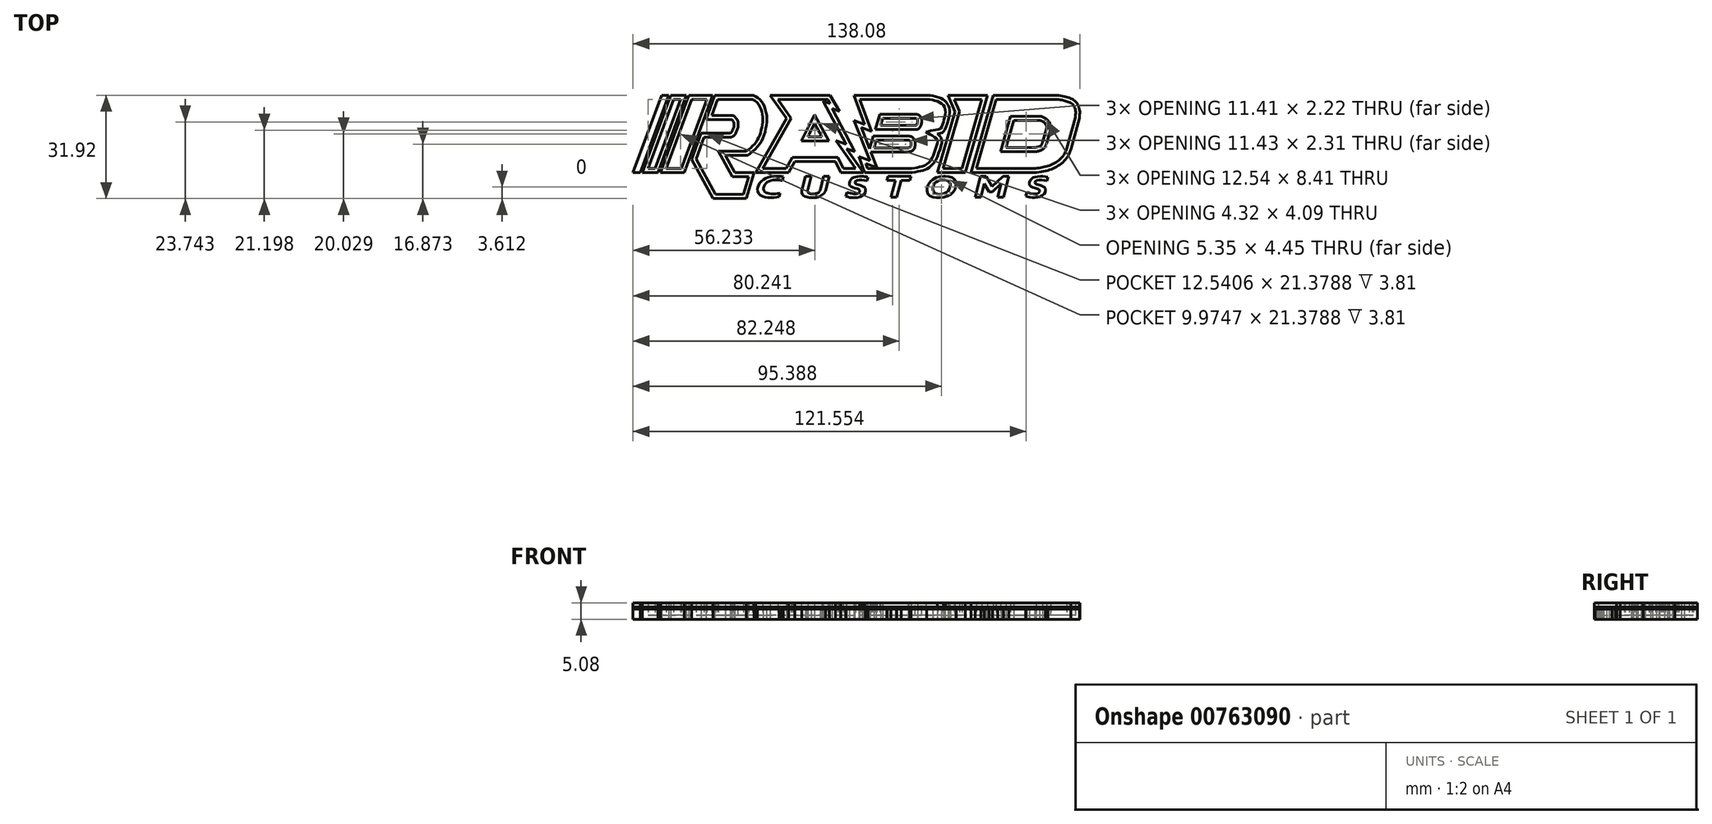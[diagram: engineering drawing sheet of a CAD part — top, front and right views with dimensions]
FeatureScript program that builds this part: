
annotation { "Feature Type Name" : "Feature", "Feature Type Description" : "" }
export const myFeature = defineFeature(function(context is Context, id is Id, definition is map)
    precondition{}
    {
        {
            var Q0;
            Q0=qCreatedBy(makeId("Top.planeOp"),FACE);
            var sketch = newSketch(context, id + "F0", { "sketchPlane" : qUnion([Q0])});
            skLineSegment(sketch, "E0", {"start": v(63.14, 15.4) * mm, "end": v(43.59, 15.4) * mm});
            skLineSegment(sketch, "E1", {"start": v(-67.72, -8.52) * mm, "end": v(-58.92, 15.4) * mm});
            skLineSegment(sketch, "E2", {"start": v(-51.92, -8.52) * mm, "end": v(-59.3, -8.52) * mm});
            skLineSegment(sketch, "E3", {"start": v(-56.72, 15.4) * mm, "end": v(-65.52, -8.52) * mm});
            skLineSegment(sketch, "E4", {"start": v(-64.84, -8.52) * mm, "end": v(-56.04, 15.4) * mm});
            skLineSegment(sketch, "E5", {"start": v(-51.23, 15.4) * mm, "end": v(-60.03, -8.52) * mm});
            skLineSegment(sketch, "E6", {"start": v(-59.3, -8.52) * mm, "end": v(-50.5, 15.4) * mm});
            skLineSegment(sketch, "E7", {"start": v(-43.12, 15.4) * mm, "end": v(-51.92, -8.52) * mm});
            skLineSegment(sketch, "E8", {"start": v(-45.2, 7.94) * mm, "end": v(-42.45, 15.4) * mm});
            skLineSegment(sketch, "E9", {"start": v(-45.2, 7.94) * mm, "end": v(-37.2, 7.94) * mm});
            skLineSegment(sketch, "E10", {"start": v(-37.63, 3.75) * mm, "end": v(-46.65, 3.75) * mm});
            skLineSegment(sketch, "E11", {"start": v(-46.65, 3.75) * mm, "end": v(-49.65, -4.39) * mm});
            skLineSegment(sketch, "E12", {"start": v(-49.65, -4.39) * mm, "end": v(-43.04, -16.52) * mm});
            skLineSegment(sketch, "E13", {"start": v(-43.04, -16.52) * mm, "end": v(-32.71, -16.52) * mm});
            skLineSegment(sketch, "E14", {"start": v(-32.71, -16.52) * mm, "end": v(-30.27, -8.46) * mm});
            skLineSegment(sketch, "E15", {"start": v(-30.27, -8.46) * mm, "end": v(-36.23, -8.46) * mm});
            skLineSegment(sketch, "E16", {"start": v(-36.23, -8.46) * mm, "end": v(-39.16, -3.08) * mm});
            skLineSegment(sketch, "E17", {"start": v(-39.16, -3.08) * mm, "end": v(-32.26, -3.08) * mm});
            skLineSegment(sketch, "E18", {"start": v(-29.78, -8.46) * mm, "end": v(-19.63, -8.46) * mm});
            skLineSegment(sketch, "E19", {"start": v(-25.33, 15.4) * mm, "end": v(-20.3, 8.28) * mm});
            skLineSegment(sketch, "E20", {"start": v(-20.3, 8.28) * mm, "end": v(-29.78, -8.46) * mm});
            skLineSegment(sketch, "E21", {"start": v(-19.63, -8.46) * mm, "end": v(-17.7, -5.04) * mm});
            skLineSegment(sketch, "E22", {"start": v(-17.7, -5.04) * mm, "end": v(-5.2, -5.04) * mm});
            skLineSegment(sketch, "E23", {"start": v(-5.2, -5.04) * mm, "end": v(-3.5, -8.46) * mm});
            skLineSegment(sketch, "E24", {"start": v(-6.75, 15.4) * mm, "end": v(-3.93, 10.47) * mm});
            skLineSegment(sketch, "E25", {"start": v(-3.93, 10.47) * mm, "end": v(-6.2, 11.32) * mm});
            skLineSegment(sketch, "E26", {"start": v(-6.2, 11.32) * mm, "end": v(0.84, -1.97) * mm});
            skLineSegment(sketch, "E27", {"start": v(0.84, -1.97) * mm, "end": v(-1.66, -1.06) * mm});
            skLineSegment(sketch, "E28", {"start": v(-1.66, -1.06) * mm, "end": v(3.5, -8.46) * mm});
            skLineSegment(sketch, "E29", {"start": v(-9.33, 2.63) * mm, "end": v(-13.65, 2.63) * mm});
            skLineSegment(sketch, "E30", {"start": v(-13.65, 2.63) * mm, "end": v(-11.6, 6.72) * mm});
            skLineSegment(sketch, "E31", {"start": v(-11.6, 6.72) * mm, "end": v(-9.33, 2.63) * mm});
            skLineSegment(sketch, "E32", {"start": v(0.59, 15.4) * mm, "end": v(3.85, 6.44) * mm});
            skLineSegment(sketch, "E33", {"start": v(3.85, 6.44) * mm, "end": v(0.55, 7.69) * mm});
            skLineSegment(sketch, "E34", {"start": v(0.55, 7.69) * mm, "end": v(5.5, -4.8) * mm});
            skLineSegment(sketch, "E35", {"start": v(5.5, -4.8) * mm, "end": v(2.03, -3.56) * mm});
            skLineSegment(sketch, "E36", {"start": v(2.03, -3.56) * mm, "end": v(3.9, -8.46) * mm});
            skLineSegment(sketch, "E37", {"start": v(9.47, 8.33) * mm, "end": v(8.82, 6.12) * mm});
            skLineSegment(sketch, "E38", {"start": v(6.8, -0.8) * mm, "end": v(17.35, -0.8) * mm});
            skLineSegment(sketch, "E39", {"start": v(7.48, 1.5) * mm, "end": v(17.6, 1.5) * mm});
            skLineSegment(sketch, "E40", {"start": v(9.47, 8.33) * mm, "end": v(19.75, 8.33) * mm});
            skLineSegment(sketch, "E41", {"start": v(8.82, 6.12) * mm, "end": v(19.5, 6.12) * mm});
            skLineSegment(sketch, "E42", {"start": v(29.63, 15.4) * mm, "end": v(31.86, 10.36) * mm});
            skLineSegment(sketch, "E43", {"start": v(31.86, 10.36) * mm, "end": v(26.4, -8.46) * mm});
            skLineSegment(sketch, "E44", {"start": v(41.79, 15.4) * mm, "end": v(34.96, -8.46) * mm});
            skLineSegment(sketch, "E45", {"start": v(43.59, 15.4) * mm, "end": v(36.77, -8.46) * mm});
            skLineSegment(sketch, "E46", {"start": v(57.72, 7.72) * mm, "end": v(49.97, 7.72) * mm});
            skLineSegment(sketch, "E47", {"start": v(49.97, 7.72) * mm, "end": v(47.56, -0.7) * mm});
            skLineSegment(sketch, "E48", {"start": v(47.56, -0.7) * mm, "end": v(56.76, -0.7) * mm});
            skLineSegment(sketch, "E49", {"start": v(60.1, 5.21) * mm, "end": v(58.87, 0.9) * mm});
            skFitSpline(sketch, "E50", {"points": [v(70.23, 8.37) * mm, v(70.23, 11.3) * mm, v(68.98, 13.62) * mm, v(67.2, 14.63) * mm, v(63.14, 15.4) * mm], "startDerivative": vector(1.44, 11.8) * mm, "endDerivative": vector(-15.36, 0) * mm});
            skLineSegment(sketch, "E51", {"start": v(70.23, 8.37) * mm, "end": v(67.61, -1.4) * mm});
            skFitSpline(sketch, "E52", {"points": [v(26.31, 3.48) * mm, v(27.66, 3.78) * mm, v(28.6, 4.72) * mm, v(30.1, 9.84) * mm, v(29.74, 12.25) * mm, v(28.71, 13.68) * mm, v(26.6, 14.85) * mm, v(23.32, 15.4) * mm], "startDerivative": vector(12.7, 2.15) * mm, "endDerivative": vector(-17.65, 0) * mm});
            skFitSpline(sketch, "E53", {"points": [v(26.31, 3.48) * mm, v(27.17, 2.79) * mm, v(27.7, 1.55) * mm, v(27.61, 0.35) * mm, v(25.8, -4.7) * mm, v(24.38, -6.43) * mm, v(22.74, -7.53) * mm, v(20.7, -8.07) * mm, v(17.69, -8.46) * mm], "startDerivative": vector(10.33, -6.33) * mm, "endDerivative": vector(-21.35, 0) * mm});
            skFitSpline(sketch, "E54", {"points": [v(19.75, 8.33) * mm, v(20.01, 8.2) * mm, v(20.22, 7.86) * mm, v(20.1, 6.56) * mm, v(19.95, 6.28) * mm, v(19.5, 6.12) * mm], "startDerivative": vector(1.94, 0) * mm, "endDerivative": vector(-2.82, 0) * mm});
            skFitSpline(sketch, "E55", {"points": [v(17.6, 1.5) * mm, v(17.93, 1.37) * mm, v(18.17, 0.96) * mm, v(18.18, -0.17) * mm, v(17.97, -0.55) * mm, v(17.35, -0.8) * mm], "startDerivative": vector(2.34, 0) * mm, "endDerivative": vector(-5.47, -0.56) * mm});
            skFitSpline(sketch, "E56", {"points": [v(-30.5, 15.4) * mm, v(-28.7, 14.3) * mm, v(-27.34, 12.4) * mm, v(-26.4, 9.2) * mm, v(-26.57, 5.78) * mm, v(-27.6, 2.09) * mm, v(-29.64, -0.93) * mm, v(-32.26, -3.08) * mm], "startDerivative": vector(16.3, -8.18) * mm, "endDerivative": vector(-18.4, -13.35) * mm});
            skFitSpline(sketch, "E57", {"points": [v(57.72, 7.72) * mm, v(58.57, 7.52) * mm, v(59.23, 7.13) * mm, v(59.76, 6.54) * mm, v(60.1, 5.21) * mm], "startDerivative": vector(3.5, 0) * mm, "endDerivative": vector(-0.84, -6.8) * mm});
            skFitSpline(sketch, "E58", {"points": [v(56.76, -0.7) * mm, v(57.5, -0.52) * mm, v(58.2, -0.25) * mm, v(58.63, 0.26) * mm, v(58.87, 0.9) * mm], "startDerivative": vector(2.87, 0.64) * mm, "endDerivative": vector(0.84, 2.68) * mm});
            skLineSegment(sketch, "E59.trimOffspring", {"start": v(-56.72, 15.4) * mm, "end": v(-58.92, 15.4) * mm});
            skLineSegment(sketch, "E60.trimOffspring", {"start": v(-51.23, 15.4) * mm, "end": v(-56.04, 15.4) * mm});
            skLineSegment(sketch, "E61.trimOffspring", {"start": v(-43.12, 15.4) * mm, "end": v(-50.5, 15.4) * mm});
            skLineSegment(sketch, "E62.trimOffspring", {"start": v(-30.5, 15.4) * mm, "end": v(-42.45, 15.4) * mm});
            skLineSegment(sketch, "E63.trimOffspring", {"start": v(-60.03, -8.52) * mm, "end": v(-64.84, -8.52) * mm});
            skLineSegment(sketch, "E64.trimOffspring", {"start": v(-65.52, -8.52) * mm, "end": v(-67.72, -8.52) * mm});
            skLineSegment(sketch, "E65.trimOffspring", {"start": v(-3.5, -8.46) * mm, "end": v(3.5, -8.46) * mm});
            skLineSegment(sketch, "E66.trimOffspring", {"start": v(3.9, -8.46) * mm, "end": v(17.69, -8.46) * mm});
            skLineSegment(sketch, "E67.trimOffspring", {"start": v(-6.75, 15.4) * mm, "end": v(-25.33, 15.4) * mm});
            skLineSegment(sketch, "E68.trimOffspring", {"start": v(7.48, 1.5) * mm, "end": v(6.8, -0.8) * mm});
            skLineSegment(sketch, "E69.trimOffspring", {"start": v(23.32, 15.4) * mm, "end": v(0.59, 15.4) * mm});
            skLineSegment(sketch, "E70.trimOffspring", {"start": v(26.4, -8.46) * mm, "end": v(34.96, -8.46) * mm});
            skLineSegment(sketch, "E71.trimOffspring", {"start": v(36.77, -8.46) * mm, "end": v(56.13, -8.46) * mm});
            skLineSegment(sketch, "E72.trimOffspring", {"start": v(41.79, 15.4) * mm, "end": v(29.63, 15.4) * mm});
            skFitSpline(sketch, "E73", {"points": [v(67.61, -1.4) * mm, v(66.86, -3.06) * mm, v(65.63, -4.79) * mm, v(63.85, -6.28) * mm, v(61.91, -7.32) * mm, v(59.62, -7.97) * mm, v(56.13, -8.46) * mm], "startDerivative": vector(-4.7, -11.34) * mm, "endDerivative": vector(-18.16, 0) * mm});
            skLineSegment(sketch, "E74", {"start": v(-21.23, -9.76) * mm, "end": v(-21.5, -10.99) * mm});
            skFitSpline(sketch, "E75", {"points": [v(-21.5, -10.99) * mm, v(-22.97, -10.72) * mm, v(-24.28, -10.74) * mm, v(-25.85, -11.2) * mm, v(-27, -12.23) * mm, v(-27.37, -13.14) * mm, v(-27.28, -13.97) * mm, v(-26.77, -14.6) * mm, v(-25.82, -14.94) * mm, v(-24.18, -15.08) * mm, v(-22.33, -14.83) * mm], "startDerivative": vector(-13.97, 2.96) * mm, "endDerivative": vector(15.34, 2.82) * mm});
            skFitSpline(sketch, "E76", {"points": [v(-21.23, -9.76) * mm, v(-22.2, -9.6) * mm, v(-23.42, -9.55) * mm, v(-24.64, -9.6) * mm, v(-26.04, -9.93) * mm, v(-26.99, -10.35) * mm, v(-27.96, -11) * mm, v(-28.75, -12) * mm, v(-29.08, -12.73) * mm, v(-29.23, -13.4) * mm, v(-29.15, -14.32) * mm, v(-28.73, -15.14) * mm, v(-27.9, -15.77) * mm, v(-26.68, -16.15) * mm, v(-25.33, -16.25) * mm, v(-23.8, -16.2) * mm, v(-22.58, -15.95) * mm], "startDerivative": vector(-16.16, 3.13) * mm, "endDerivative": vector(17.8, 4.48) * mm});
            skLineSegment(sketch, "E77.trimOffspring", {"start": v(-22.33, -14.83) * mm, "end": v(-22.58, -15.95) * mm});
            skLineSegment(sketch, "E78", {"start": v(-14.42, -9.63) * mm, "end": v(-12.66, -9.63) * mm});
            skLineSegment(sketch, "E79", {"start": v(12.2, -16.1) * mm, "end": v(13.8, -16.1) * mm});
            skLineSegment(sketch, "E80", {"start": v(-14.42, -9.63) * mm, "end": v(-15.45, -13.6) * mm});
            skLineSegment(sketch, "E81", {"start": v(-12.66, -9.63) * mm, "end": v(-13.72, -13.7) * mm});
            skLineSegment(sketch, "E82", {"start": v(-8.8, -9.63) * mm, "end": v(-9.9, -13.88) * mm});
            skLineSegment(sketch, "E83", {"start": v(-7.1, -9.63) * mm, "end": v(-8.22, -14.01) * mm});
            skFitSpline(sketch, "E84", {"points": [v(-15.45, -13.6) * mm, v(-15.56, -14.25) * mm, v(-15.45, -14.91) * mm, v(-15.19, -15.4) * mm, v(-14.47, -15.9) * mm, v(-13.08, -16.2) * mm, v(-11.72, -16.22) * mm, v(-10.7, -16.06) * mm, v(-9.8, -15.69) * mm, v(-8.93, -15.06) * mm, v(-8.47, -14.55) * mm, v(-8.22, -14.01) * mm], "startDerivative": vector(-1.99, -8.13) * mm, "endDerivative": vector(2.8, 7.52) * mm});
            skFitSpline(sketch, "E85", {"points": [v(-13.72, -13.7) * mm, v(-13.77, -13.94) * mm, v(-13.77, -14.2) * mm, v(-13.72, -14.43) * mm, v(-13.43, -14.76) * mm, v(-12.93, -14.99) * mm, v(-11.88, -15.05) * mm, v(-11.08, -14.96) * mm, v(-10.47, -14.73) * mm, v(-10.11, -14.34) * mm, v(-9.9, -13.88) * mm], "startDerivative": vector(-0.84, -3.35) * mm, "endDerivative": vector(1.84, 4.68) * mm});
            skLineSegment(sketch, "E86.trimOffspring", {"start": v(-8.8, -9.63) * mm, "end": v(-7.1, -9.63) * mm});
            skLineSegment(sketch, "E87", {"start": v(4.85, -9.89) * mm, "end": v(4.6, -11.04) * mm});
            skFitSpline(sketch, "E88", {"points": [v(4.6, -11.04) * mm, v(3.56, -10.81) * mm, v(2.6, -10.7) * mm, v(1.85, -10.74) * mm, v(1.26, -10.94) * mm, v(1, -11.17) * mm, v(0.94, -11.35) * mm, v(0.93, -11.6) * mm, v(1.06, -11.85) * mm, v(1.45, -12.06) * mm, v(2.83, -12.5) * mm, v(3.5, -12.8) * mm, v(3.91, -13.1) * mm, v(4.11, -13.37) * mm, v(4.17, -13.67) * mm, v(4.17, -14.01) * mm, v(4.02, -14.62) * mm, v(3.54, -15.3) * mm, v(2.88, -15.77) * mm, v(2.05, -16.06) * mm, v(0.97, -16.24) * mm, v(0.23, -16.27) * mm, v(-0.68, -16.14) * mm, v(-1.44, -15.96) * mm, v(-1.98, -15.77) * mm], "startDerivative": vector(-19.24, 4.6) * mm, "endDerivative": vector(-13.06, 4.98) * mm});
            skFitSpline(sketch, "E89", {"points": [v(4.85, -9.89) * mm, v(4.17, -9.74) * mm, v(3.28, -9.63) * mm, v(2.3, -9.63) * mm, v(1.36, -9.74) * mm, v(0.64, -9.93) * mm, v(0.14, -10.19) * mm, v(-0.27, -10.55) * mm, v(-0.68, -11.1) * mm, v(-0.87, -11.73) * mm, v(-0.72, -12.43) * mm, v(-0.15, -12.87) * mm, v(0.52, -13.13) * mm, v(1.58, -13.47) * mm, v(2.06, -13.67) * mm, v(2.33, -14) * mm, v(2.36, -14.28) * mm, v(2.25, -14.6) * mm, v(1.98, -14.81) * mm, v(1.59, -14.98) * mm, v(0.9, -15.06) * mm, v(0.29, -15.02) * mm, v(-0.54, -14.88) * mm, v(-1.25, -14.69) * mm, v(-1.63, -14.5) * mm], "startDerivative": vector(-14.34, 3.67) * mm, "endDerivative": vector(-10.03, 5.5) * mm});
            skLineSegment(sketch, "E90", {"start": v(-1.63, -14.5) * mm, "end": v(-1.98, -15.77) * mm});
            skLineSegment(sketch, "E91", {"start": v(60.47, -9.88) * mm, "end": v(60.23, -11.03) * mm});
            skFitSpline(sketch, "E92", {"points": [v(60.23, -11.03) * mm, v(59.18, -10.8) * mm, v(58.22, -10.69) * mm, v(57.47, -10.73) * mm, v(56.88, -10.93) * mm, v(56.62, -11.16) * mm, v(56.56, -11.34) * mm, v(56.55, -11.6) * mm, v(56.68, -11.84) * mm, v(57.07, -12.06) * mm, v(58.45, -12.5) * mm, v(59.12, -12.8) * mm, v(59.53, -13.08) * mm, v(59.73, -13.36) * mm, v(59.79, -13.67) * mm, v(59.79, -14) * mm, v(59.64, -14.61) * mm, v(59.16, -15.29) * mm, v(58.5, -15.76) * mm, v(57.67, -16.06) * mm, v(56.59, -16.24) * mm, v(55.85, -16.26) * mm, v(54.94, -16.13) * mm, v(54.19, -15.95) * mm, v(53.64, -15.76) * mm], "startDerivative": vector(-19.24, 4.6) * mm, "endDerivative": vector(-13.06, 4.98) * mm});
            skFitSpline(sketch, "E93", {"points": [v(60.47, -9.88) * mm, v(59.79, -9.73) * mm, v(58.9, -9.62) * mm, v(57.92, -9.62) * mm, v(56.98, -9.73) * mm, v(56.26, -9.92) * mm, v(55.76, -10.18) * mm, v(55.35, -10.54) * mm, v(54.94, -11.1) * mm, v(54.75, -11.73) * mm, v(54.9, -12.43) * mm, v(55.47, -12.86) * mm, v(56.14, -13.12) * mm, v(57.2, -13.46) * mm, v(57.68, -13.67) * mm, v(57.95, -14) * mm, v(57.99, -14.27) * mm, v(57.87, -14.6) * mm, v(57.6, -14.8) * mm, v(57.2, -14.97) * mm, v(56.52, -15.05) * mm, v(55.91, -15) * mm, v(55.08, -14.87) * mm, v(54.37, -14.68) * mm, v(54, -14.5) * mm], "startDerivative": vector(-14.34, 3.67) * mm, "endDerivative": vector(-10.03, 5.5) * mm});
            skLineSegment(sketch, "E94", {"start": v(54, -14.5) * mm, "end": v(53.64, -15.76) * mm});
            skLineSegment(sketch, "E95", {"start": v(11.08, -9.63) * mm, "end": v(10.77, -10.85) * mm});
            skLineSegment(sketch, "E96", {"start": v(10.77, -10.85) * mm, "end": v(13.42, -10.85) * mm});
            skLineSegment(sketch, "E97", {"start": v(13.42, -10.85) * mm, "end": v(12.02, -16.1) * mm});
            skLineSegment(sketch, "E98", {"start": v(12.02, -16.1) * mm, "end": v(12.2, -16.1) * mm});
            skLineSegment(sketch, "E99", {"start": v(13.8, -16.1) * mm, "end": v(15.2, -10.85) * mm});
            skLineSegment(sketch, "E100", {"start": v(15.2, -10.85) * mm, "end": v(17.86, -10.85) * mm});
            skLineSegment(sketch, "E101", {"start": v(17.86, -10.85) * mm, "end": v(18.16, -9.63) * mm});
            skFitSpline(sketch, "E102", {"points": [v(27.98, -10.68) * mm, v(27.19, -10.76) * mm, v(26.47, -11.02) * mm, v(25.85, -11.42) * mm, v(25.4, -11.93) * mm, v(25.08, -12.64) * mm, v(24.92, -13.24) * mm, v(24.96, -14) * mm, v(25.34, -14.58) * mm, v(25.9, -14.94) * mm, v(26.64, -15.1) * mm, v(27.47, -15.13) * mm, v(28.26, -14.98) * mm, v(29.06, -14.64) * mm, v(29.68, -14.13) * mm, v(30.1, -13.5) * mm, v(30.34, -12.7) * mm, v(30.37, -12.02) * mm, v(30.16, -11.45) * mm, v(29.8, -11.09) * mm, v(29.2, -10.83) * mm, v(28.61, -10.7) * mm, v(27.98, -10.68) * mm]});
            skFitSpline(sketch, "E103", {"points": [v(28.21, -9.63) * mm, v(27.44, -9.67) * mm, v(26.74, -9.79) * mm, v(25.84, -10.1) * mm, v(25.14, -10.46) * mm, v(24.5, -10.9) * mm, v(24.01, -11.4) * mm, v(23.65, -11.96) * mm, v(23.35, -12.55) * mm, v(23.16, -13.25) * mm, v(23.1, -13.88) * mm, v(23.2, -14.57) * mm, v(23.4, -15.05) * mm, v(23.77, -15.47) * mm, v(24.22, -15.73) * mm, v(24.84, -15.98) * mm, v(25.5, -16.1) * mm, v(26.21, -16.15) * mm, v(27.08, -16.16) * mm, v(27.82, -16.14) * mm, v(28.85, -15.98) * mm, v(29.51, -15.73) * mm, v(30.26, -15.31) * mm, v(30.74, -15) * mm, v(31.25, -14.48) * mm, v(31.62, -13.96) * mm, v(31.88, -13.45) * mm, v(32.09, -12.75) * mm, v(32.2, -11.83) * mm, v(32.03, -11.08) * mm, v(31.72, -10.64) * mm, v(31.26, -10.26) * mm, v(30.72, -9.98) * mm, v(30.04, -9.77) * mm, v(29.55, -9.68) * mm, v(28.95, -9.63) * mm, v(28.21, -9.63) * mm]});
            skLineSegment(sketch, "E104", {"start": v(39.69, -9.63) * mm, "end": v(38.06, -16.1) * mm});
            skLineSegment(sketch, "E105", {"start": v(40.82, -11.93) * mm, "end": v(39.76, -16.1) * mm});
            skLineSegment(sketch, "E106", {"start": v(41.43, -9.63) * mm, "end": v(43.29, -12.74) * mm});
            skLineSegment(sketch, "E107", {"start": v(43.29, -12.74) * mm, "end": v(46.71, -9.63) * mm});
            skLineSegment(sketch, "E108", {"start": v(48.4, -9.63) * mm, "end": v(46.78, -16.1) * mm});
            skLineSegment(sketch, "E109", {"start": v(40.82, -11.93) * mm, "end": v(42.29, -14.4) * mm});
            skLineSegment(sketch, "E110", {"start": v(42.29, -14.4) * mm, "end": v(43.35, -14.4) * mm});
            skLineSegment(sketch, "E111", {"start": v(43.35, -14.4) * mm, "end": v(46.08, -11.91) * mm});
            skLineSegment(sketch, "E112", {"start": v(46.08, -11.91) * mm, "end": v(45.03, -16.1) * mm});
            skLineSegment(sketch, "E113.trimOffspring", {"start": v(46.71, -9.63) * mm, "end": v(48.4, -9.63) * mm});
            skLineSegment(sketch, "E114.trimOffspring", {"start": v(45.03, -16.1) * mm, "end": v(46.78, -16.1) * mm});
            skLineSegment(sketch, "E115.trimOffspring", {"start": v(39.69, -9.63) * mm, "end": v(41.43, -9.63) * mm});
            skLineSegment(sketch, "E116.trimOffspring", {"start": v(38.06, -16.1) * mm, "end": v(39.76, -16.1) * mm});
            skLineSegment(sketch, "E117.trimOffspring", {"start": v(28.21, -9.63) * mm, "end": v(28.95, -9.63) * mm});
            skLineSegment(sketch, "E118.trimOffspring", {"start": v(11.08, -9.63) * mm, "end": v(18.16, -9.63) * mm});
            skLineSegment(sketch, "E119.trimOffspring", {"start": v(2.3, -9.63) * mm, "end": v(3.28, -9.63) * mm});
            skFitSpline(sketch, "E120", {"points": [v(-37.2, 7.94) * mm, v(-36.54, 6.97) * mm, v(-36.58, 5.6) * mm, v(-37.2, 4.16) * mm, v(-37.63, 3.75) * mm], "startDerivative": vector(3.16, -3.56) * mm, "endDerivative": vector(-2.38, -1.75) * mm});
            skSolve(sketch);
        }
        {
            var Q0;
            Q0=makeQuery(id+"F0.imprint","IMPRINT",FACE,{"disambiguationData":[TD([[makeQuery(id+"F0.imprint","IMPRINT",EDGE,{"derivedFrom":sQuery(id+"F0.wireOp",EDGE,"E1")}),-1.0]])]});
            var Q1;
            Q1=makeQuery(id+"F0.imprint","IMPRINT",FACE,{"disambiguationData":[TD([[makeQuery(id+"F0.imprint","IMPRINT",EDGE,{"derivedFrom":sQuery(id+"F0.wireOp",EDGE,"E2")}),-1.0]])]});
            var Q2;
            Q2=makeQuery(id+"F0.imprint","IMPRINT",FACE,{"disambiguationData":[TD([[makeQuery(id+"F0.imprint","IMPRINT",EDGE,{"derivedFrom":sQuery(id+"F0.wireOp",EDGE,"E4")}),-1.0]])]});
            var Q3;
            Q3=makeQuery(id+"F0.imprint","IMPRINT",FACE,{"disambiguationData":[TD([[makeQuery(id+"F0.imprint","IMPRINT",EDGE,{"derivedFrom":sQuery(id+"F0.wireOp",EDGE,"E8")}),-1.0]])]});
            var Q4;
            Q4=makeQuery(id+"F0.imprint","IMPRINT",FACE,{"disambiguationData":[TD([[makeQuery(id+"F0.imprint","IMPRINT",EDGE,{"derivedFrom":sQuery(id+"F0.wireOp",EDGE,"E42")}),1.0]])]});
            var Q5;
            Q5=makeQuery(id+"F0.imprint","IMPRINT",FACE,{"disambiguationData":[TD([[makeQuery(id+"F0.imprint","IMPRINT",EDGE,{"derivedFrom":sQuery(id+"F0.wireOp",EDGE,"E0")}),1.0]])]});
            var Q6;
            Q6=makeQuery(id+"F0.imprint","IMPRINT",FACE,{"disambiguationData":[TD([[makeQuery(id+"F0.imprint","IMPRINT",EDGE,{"derivedFrom":sQuery(id+"F0.wireOp",EDGE,"E18")}),1.0]])]});
            var Q7;
            {var subQ0=sQuery(id+"F0.wireOp",EDGE,"E119.trimOffspring");Q7=makeQuery(id+"F0.imprint","IMPRINT",FACE,{"disambiguationData":[TD([[makeQuery(id+"F0.imprint","IMPRINT",EDGE,{"derivedFrom":subQ0}),1.0]])]});}
            var Q8;
            {var subQ0=sQuery(id+"F0.wireOp",EDGE,"E117.trimOffspring");Q8=makeQuery(id+"F0.imprint","IMPRINT",FACE,{"disambiguationData":[TD([[makeQuery(id+"F0.imprint","IMPRINT",EDGE,{"derivedFrom":subQ0}),1.0]])]});}
            var Q9;
            Q9=makeQuery(id+"F0.imprint","IMPRINT",FACE,{"disambiguationData":[TD([[makeQuery(id+"F0.imprint","IMPRINT",EDGE,{"derivedFrom":sQuery(id+"F0.wireOp",EDGE,"E32")}),1.0]])]});
            extrude(context, id + "F1", {"entities" : qUnion([Q0, Q1, Q2, Q3, Q4, Q5, Q6, Q7, Q8, Q9]), "depth" : 5.08 * mm, "offsetDistance" : 25.4 * mm});
        }
        {
            var Q0;
            Q0=makeQuery(id+"F0.imprint","IMPRINT",FACE,{"disambiguationData":[TD([[makeQuery(id+"F0.imprint","IMPRINT",EDGE,{"derivedFrom":sQuery(id+"F0.wireOp",EDGE,"E1")}),-1.0]])]});
            var Q1;
            Q1=makeQuery(id+"F0.imprint","IMPRINT",FACE,{"disambiguationData":[TD([[makeQuery(id+"F0.imprint","IMPRINT",EDGE,{"derivedFrom":sQuery(id+"F0.wireOp",EDGE,"E2")}),-1.0]])]});
            var Q2;
            Q2=makeQuery(id+"F0.imprint","IMPRINT",FACE,{"disambiguationData":[TD([[makeQuery(id+"F0.imprint","IMPRINT",EDGE,{"derivedFrom":sQuery(id+"F0.wireOp",EDGE,"E4")}),-1.0]])]});
            var Q3;
            Q3=makeQuery(id+"F0.imprint","IMPRINT",FACE,{"disambiguationData":[TD([[makeQuery(id+"F0.imprint","IMPRINT",EDGE,{"derivedFrom":sQuery(id+"F0.wireOp",EDGE,"E8")}),-1.0]])]});
            var Q4;
            Q4=makeQuery(id+"F0.imprint","IMPRINT",FACE,{"disambiguationData":[TD([[makeQuery(id+"F0.imprint","IMPRINT",EDGE,{"derivedFrom":sQuery(id+"F0.wireOp",EDGE,"E42")}),1.0]])]});
            var Q5;
            Q5=makeQuery(id+"F0.imprint","IMPRINT",FACE,{"disambiguationData":[TD([[makeQuery(id+"F0.imprint","IMPRINT",EDGE,{"derivedFrom":sQuery(id+"F0.wireOp",EDGE,"E0")}),1.0]])]});
            var Q6;
            Q6=makeQuery(id+"F0.imprint","IMPRINT",FACE,{"disambiguationData":[TD([[makeQuery(id+"F0.imprint","IMPRINT",EDGE,{"derivedFrom":sQuery(id+"F0.wireOp",EDGE,"E18")}),1.0]])]});
            var Q7;
            {var subQ0=sQuery(id+"F0.wireOp",EDGE,"E119.trimOffspring");Q7=makeQuery(id+"F0.imprint","IMPRINT",FACE,{"disambiguationData":[TD([[makeQuery(id+"F0.imprint","IMPRINT",EDGE,{"derivedFrom":subQ0}),1.0]])]});}
            var Q8;
            {var subQ0=sQuery(id+"F0.wireOp",EDGE,"E117.trimOffspring");Q8=makeQuery(id+"F0.imprint","IMPRINT",FACE,{"disambiguationData":[TD([[makeQuery(id+"F0.imprint","IMPRINT",EDGE,{"derivedFrom":subQ0}),1.0]])]});}
            var Q9;
            Q9=makeQuery(id+"F0.imprint","IMPRINT",FACE,{"disambiguationData":[TD([[makeQuery(id+"F0.imprint","IMPRINT",EDGE,{"derivedFrom":sQuery(id+"F0.wireOp",EDGE,"E32")}),1.0]])]});
            extrude(context, id + "F2", {"entities" : qUnion([Q0, Q1, Q2, Q3, Q4, Q5, Q6, Q7, Q8, Q9]), "depth" : 3.8 * mm, "offsetDistance" : 25.4 * mm});
        }
        {
            var Q0;
            Q0=makeQuery(id+"F1.opExtrude","CAP_FACE",FACE,{"disambiguationData":[OSD([sQuery(id+"F0.wireOp",EDGE,"E8"),sQuery(id+"F0.wireOp",EDGE,"E9"),sQuery(id+"F0.wireOp",EDGE,"E10"),sQuery(id+"F0.wireOp",EDGE,"E11"),sQuery(id+"F0.wireOp",EDGE,"E12"),sQuery(id+"F0.wireOp",EDGE,"E13"),sQuery(id+"F0.wireOp",EDGE,"E14"),sQuery(id+"F0.wireOp",EDGE,"E15"),sQuery(id+"F0.wireOp",EDGE,"E16"),sQuery(id+"F0.wireOp",EDGE,"E17"),sQuery(id+"F0.wireOp",EDGE,"E56"),sQuery(id+"F0.wireOp",EDGE,"E62.trimOffspring"),sQuery(id+"F0.wireOp",EDGE,"E120")])],"isStart":false});
            var Q1;
            Q1=makeQuery(id+"F1.opExtrude","CAP_FACE",FACE,{"disambiguationData":[OSD([sQuery(id+"F0.wireOp",EDGE,"E18"),sQuery(id+"F0.wireOp",EDGE,"E19"),sQuery(id+"F0.wireOp",EDGE,"E20"),sQuery(id+"F0.wireOp",EDGE,"E21"),sQuery(id+"F0.wireOp",EDGE,"E22"),sQuery(id+"F0.wireOp",EDGE,"E23"),sQuery(id+"F0.wireOp",EDGE,"E24"),sQuery(id+"F0.wireOp",EDGE,"E25"),sQuery(id+"F0.wireOp",EDGE,"E26"),sQuery(id+"F0.wireOp",EDGE,"E27"),sQuery(id+"F0.wireOp",EDGE,"E28"),sQuery(id+"F0.wireOp",EDGE,"E29"),sQuery(id+"F0.wireOp",EDGE,"E30"),sQuery(id+"F0.wireOp",EDGE,"E31"),sQuery(id+"F0.wireOp",EDGE,"E65.trimOffspring"),sQuery(id+"F0.wireOp",EDGE,"E67.trimOffspring")])],"isStart":false});
            var Q2;
            Q2=makeQuery(id+"F1.opExtrude","CAP_FACE",FACE,{"disambiguationData":[OSD([sQuery(id+"F0.wireOp",EDGE,"E32"),sQuery(id+"F0.wireOp",EDGE,"E33"),sQuery(id+"F0.wireOp",EDGE,"E34"),sQuery(id+"F0.wireOp",EDGE,"E35"),sQuery(id+"F0.wireOp",EDGE,"E36"),sQuery(id+"F0.wireOp",EDGE,"E37"),sQuery(id+"F0.wireOp",EDGE,"E38"),sQuery(id+"F0.wireOp",EDGE,"E39"),sQuery(id+"F0.wireOp",EDGE,"E40"),sQuery(id+"F0.wireOp",EDGE,"E41"),sQuery(id+"F0.wireOp",EDGE,"E52"),sQuery(id+"F0.wireOp",EDGE,"E53"),sQuery(id+"F0.wireOp",EDGE,"E54"),sQuery(id+"F0.wireOp",EDGE,"E55"),sQuery(id+"F0.wireOp",EDGE,"E66.trimOffspring"),sQuery(id+"F0.wireOp",EDGE,"E68.trimOffspring"),sQuery(id+"F0.wireOp",EDGE,"E69.trimOffspring")])],"isStart":false});
            var Q3;
            Q3=makeQuery(id+"F1.opExtrude","CAP_FACE",FACE,{"disambiguationData":[OSD([sQuery(id+"F0.wireOp",EDGE,"E42"),sQuery(id+"F0.wireOp",EDGE,"E43"),sQuery(id+"F0.wireOp",EDGE,"E44"),sQuery(id+"F0.wireOp",EDGE,"E70.trimOffspring"),sQuery(id+"F0.wireOp",EDGE,"E72.trimOffspring")])],"isStart":false});
            var Q4;
            Q4=makeQuery(id+"F1.opExtrude","CAP_FACE",FACE,{"disambiguationData":[OSD([sQuery(id+"F0.wireOp",EDGE,"E0"),sQuery(id+"F0.wireOp",EDGE,"E45"),sQuery(id+"F0.wireOp",EDGE,"E46"),sQuery(id+"F0.wireOp",EDGE,"E47"),sQuery(id+"F0.wireOp",EDGE,"E48"),sQuery(id+"F0.wireOp",EDGE,"E49"),sQuery(id+"F0.wireOp",EDGE,"E50"),sQuery(id+"F0.wireOp",EDGE,"E51"),sQuery(id+"F0.wireOp",EDGE,"E57"),sQuery(id+"F0.wireOp",EDGE,"E58"),sQuery(id+"F0.wireOp",EDGE,"E71.trimOffspring"),sQuery(id+"F0.wireOp",EDGE,"E73")])],"isStart":false});
            var Q5;
            Q5=makeQuery(id+"F1.opExtrude","CAP_FACE",FACE,{"disambiguationData":[OSD([sQuery(id+"F0.wireOp",EDGE,"E2"),sQuery(id+"F0.wireOp",EDGE,"E6"),sQuery(id+"F0.wireOp",EDGE,"E7"),sQuery(id+"F0.wireOp",EDGE,"E61.trimOffspring")])],"isStart":false});
            var Q6;
            Q6=makeQuery(id+"F1.opExtrude","CAP_FACE",FACE,{"disambiguationData":[OSD([sQuery(id+"F0.wireOp",EDGE,"E4"),sQuery(id+"F0.wireOp",EDGE,"E5"),sQuery(id+"F0.wireOp",EDGE,"E60.trimOffspring"),sQuery(id+"F0.wireOp",EDGE,"E63.trimOffspring")])],"isStart":false});
            shell(context, id + "F3", {"entities" : qUnion([Q0, Q1, Q2, Q3, Q4, Q5, Q6]), "thickness" : 1.27 * mm});
        }
        {
            var Q0;
            Q0=qSketchRegion(id+"F0",true);
            extrude(context, id + "F4", {"entities" : qUnion([Q0]), "depth" : 3.17 * mm, "offsetDistance" : 25.4 * mm});
        }
    });
